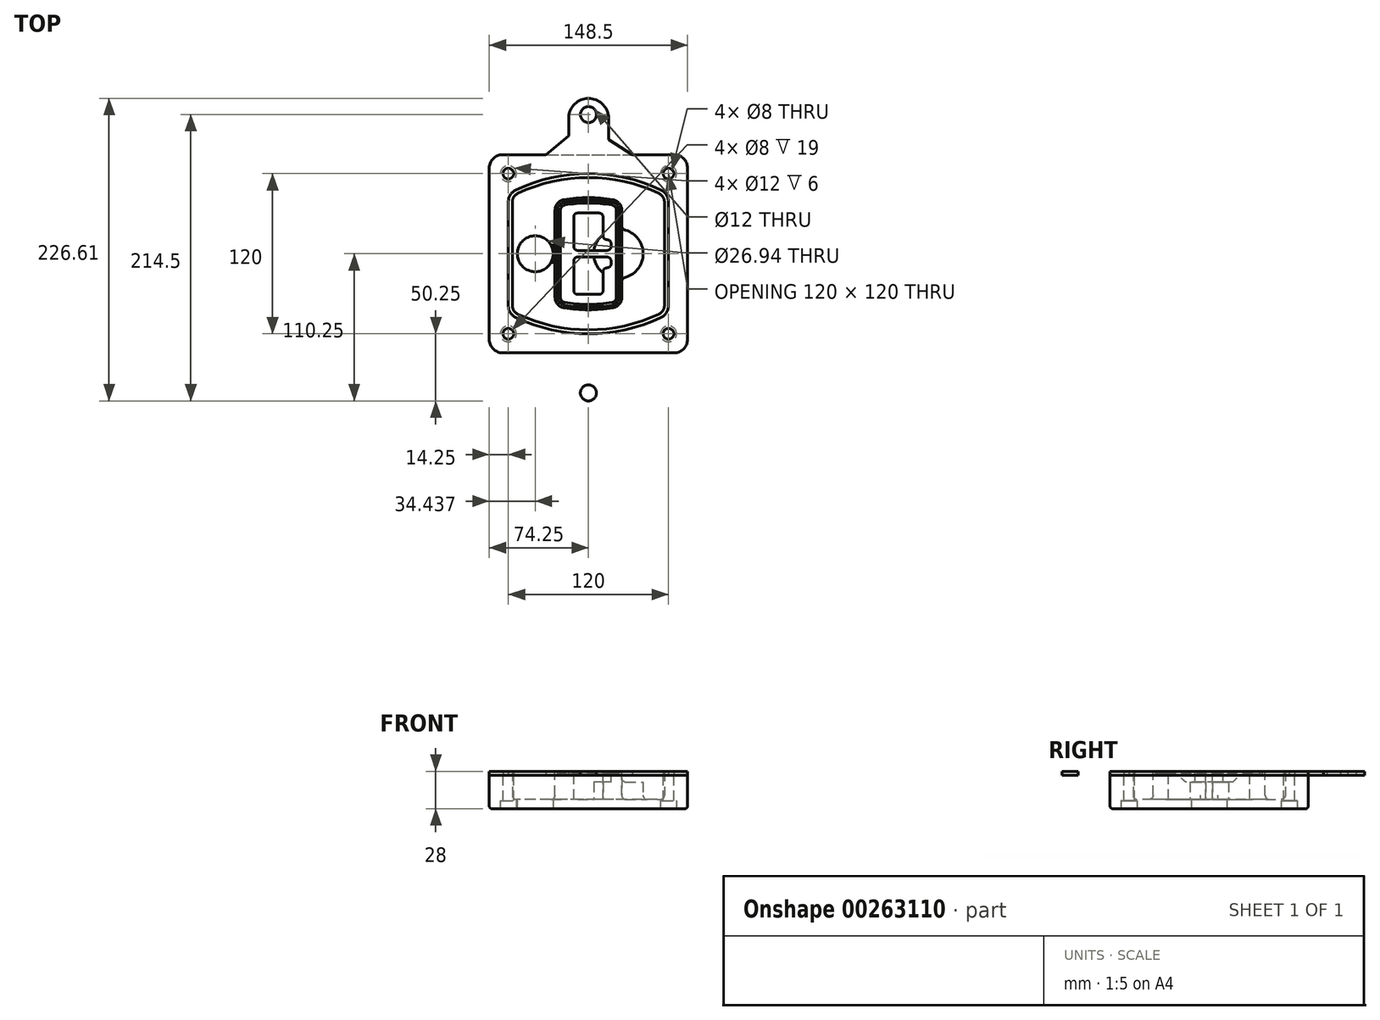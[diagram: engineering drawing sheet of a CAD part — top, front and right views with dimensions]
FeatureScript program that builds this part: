
annotation { "Feature Type Name" : "Feature", "Feature Type Description" : "" }
export const myFeature = defineFeature(function(context is Context, id is Id, definition is map)
    precondition{}
    {
        {
            var Q0;
            Q0=qCreatedBy(makeId("Top.planeOp"),FACE);
            var sketch = newSketch(context, id + "F0", { "sketchPlane" : qUnion([Q0])});
            skPoint(sketch, "E0.rect.middle", {"position": v(0, 0) * mm});
            skLineSegment(sketch, "E1.bottom", {"start": v(-64.25, -74.25) * mm, "end": v(64.25, -74.25) * mm});
            skLineSegment(sketch, "E1.top", {"start": v(-64.25, 74.25) * mm, "end": v(64.25, 74.25) * mm});
            skLineSegment(sketch, "E1.left", {"start": v(-74.25, -64.25) * mm, "end": v(-74.25, 64.25) * mm});
            skLineSegment(sketch, "E1.right", {"start": v(74.25, -64.25) * mm, "end": v(74.25, 64.25) * mm});
            skLineSegment(sketch, "E2", {"start": v(-74.25, 74.25) * mm, "end": v(74.25, -74.25) * mm, "construction": true});
            skLineSegment(sketch, "E3", {"start": v(74.25, 74.25) * mm, "end": v(-74.25, -74.25) * mm, "construction": true});
            skCircle(sketch, "E4", {"center": v(-60, 60) * mm, "radius": 4 * mm});
            skCircle(sketch, "E5", {"center": v(60, 60) * mm, "radius": 4 * mm});
            skCircle(sketch, "E6", {"center": v(60, -60) * mm, "radius": 4 * mm});
            skCircle(sketch, "E7", {"center": v(-60, -60) * mm, "radius": 4 * mm});
            skLineSegment(sketch, "E8", {"start": v(-60, 60) * mm, "end": v(60, 60) * mm, "construction": true});
            skLineSegment(sketch, "E9", {"start": v(60, 60) * mm, "end": v(60, -60) * mm, "construction": true});
            skLineSegment(sketch, "E10", {"start": v(60, -60) * mm, "end": v(-60, -60) * mm, "construction": true});
            skLineSegment(sketch, "E11", {"start": v(-60, -60) * mm, "end": v(-60, 60) * mm, "construction": true});
            skLineSegment(sketch, "E12", {"start": v(-60, 38.83) * mm, "end": v(-60, -38.83) * mm});
            skLineSegment(sketch, "E13", {"start": v(60, 38.83) * mm, "end": v(60, -38.83) * mm});
            skArc(sketch, "E14", {"start": v(54.26, 47.88) * mm, "mid": v(0, 60) * mm, "end": v(-54.26, 47.88) * mm});
            skArc(sketch, "E15", {"start": v(-54.26, -47.88) * mm, "mid": v(0, -60) * mm, "end": v(54.26, -47.88) * mm});
            skLineSegment(sketch, "E16", {"start": v(-60, 0) * mm, "end": v(60, 0) * mm, "construction": true});
            skPoint(sketch, "E17.visualSharp", {"position": v(-60, -45) * mm});
            skArc(sketch, "E17.filletArc", {"start": v(-60, -38.83) * mm, "mid": v(-58.44, -44.2) * mm, "end": v(-54.26, -47.88) * mm});
            skPoint(sketch, "E18.visualSharp", {"position": v(-60, 45) * mm});
            skArc(sketch, "E18.filletArc", {"start": v(-54.26, 47.88) * mm, "mid": v(-58.44, 44.2) * mm, "end": v(-60, 38.83) * mm});
            skPoint(sketch, "E19.visualSharp", {"position": v(60, 45) * mm});
            skArc(sketch, "E19.filletArc", {"start": v(60, 38.83) * mm, "mid": v(58.44, 44.2) * mm, "end": v(54.26, 47.88) * mm});
            skPoint(sketch, "E20.visualSharp", {"position": v(60, -45) * mm});
            skArc(sketch, "E20.filletArc", {"start": v(54.26, -47.88) * mm, "mid": v(58.44, -44.2) * mm, "end": v(60, -38.83) * mm});
            skPoint(sketch, "E21.visualSharp", {"position": v(-74.25, 74.25) * mm});
            skArc(sketch, "E21.filletArc", {"start": v(-64.25, 74.25) * mm, "mid": v(-71.32, 71.32) * mm, "end": v(-74.25, 64.25) * mm});
            skPoint(sketch, "E22.visualSharp", {"position": v(74.25, 74.25) * mm});
            skArc(sketch, "E22.filletArc", {"start": v(74.25, 64.25) * mm, "mid": v(71.32, 71.32) * mm, "end": v(64.25, 74.25) * mm});
            skPoint(sketch, "E23.visualSharp", {"position": v(74.25, -74.25) * mm});
            skArc(sketch, "E23.filletArc", {"start": v(64.25, -74.25) * mm, "mid": v(71.32, -71.32) * mm, "end": v(74.25, -64.25) * mm});
            skPoint(sketch, "E24.visualSharp", {"position": v(-74.25, -74.25) * mm});
            skArc(sketch, "E24.filletArc", {"start": v(-74.25, -64.25) * mm, "mid": v(-71.32, -71.32) * mm, "end": v(-64.25, -74.25) * mm});
            skArc(sketch, "E25.0", {"start": v(57, 38.83) * mm, "mid": v(55.9, 42.58) * mm, "end": v(52.98, 45.17) * mm});
            skLineSegment(sketch, "E25.1", {"start": v(57, 38.83) * mm, "end": v(57, -38.83) * mm});
            skArc(sketch, "E25.2", {"start": v(52.98, -45.17) * mm, "mid": v(55.9, -42.58) * mm, "end": v(57, -38.83) * mm});
            skArc(sketch, "E25.3", {"start": v(-52.98, -45.17) * mm, "mid": v(0, -57) * mm, "end": v(52.98, -45.17) * mm});
            skArc(sketch, "E25.4", {"start": v(-57, -38.83) * mm, "mid": v(-55.9, -42.58) * mm, "end": v(-52.98, -45.17) * mm});
            skArc(sketch, "E25.5", {"start": v(52.98, 45.17) * mm, "mid": v(0, 57) * mm, "end": v(-52.98, 45.17) * mm});
            skLineSegment(sketch, "E25.6", {"start": v(-57, 38.83) * mm, "end": v(-57, -38.83) * mm});
            skArc(sketch, "E25.7", {"start": v(-52.98, 45.17) * mm, "mid": v(-55.9, 42.58) * mm, "end": v(-57, 38.83) * mm});
            skArc(sketch, "E26.0", {"start": v(-55.96, 51.5) * mm, "mid": v(-61.82, 46.33) * mm, "end": v(-64, 38.83) * mm});
            skArc(sketch, "E26.1", {"start": v(55.96, 51.5) * mm, "mid": v(0, 64) * mm, "end": v(-55.96, 51.5) * mm});
            skArc(sketch, "E26.2", {"start": v(64, 38.83) * mm, "mid": v(61.82, 46.33) * mm, "end": v(55.96, 51.5) * mm});
            skLineSegment(sketch, "E26.3", {"start": v(64, 38.83) * mm, "end": v(64, -38.83) * mm});
            skArc(sketch, "E26.4", {"start": v(55.96, -51.5) * mm, "mid": v(61.82, -46.33) * mm, "end": v(64, -38.83) * mm});
            skLineSegment(sketch, "E26.5", {"start": v(-64, 38.83) * mm, "end": v(-64, -38.83) * mm});
            skArc(sketch, "E26.6", {"start": v(-55.96, -51.5) * mm, "mid": v(0, -64) * mm, "end": v(55.96, -51.5) * mm});
            skArc(sketch, "E26.7", {"start": v(-64, -38.83) * mm, "mid": v(-61.82, -46.33) * mm, "end": v(-55.96, -51.5) * mm});
            skSolve(sketch);
        }
        {
            var Q0;
            Q0=makeQuery(id+"F0.imprint","IMPRINT",FACE,{"disambiguationData":[TD([[makeQuery(id+"F0.imprint","IMPRINT",EDGE,{"derivedFrom":sQuery(id+"F0.wireOp",EDGE,"E1.bottom")}),1.0]])]});
            var Q1;
            Q1=makeQuery(id+"F0.imprint","IMPRINT",FACE,{"disambiguationData":[TD([[makeQuery(id+"F0.imprint","IMPRINT",EDGE,{"derivedFrom":sQuery(id+"F0.wireOp",EDGE,"E12")}),1.0]])]});
            var Q2;
            Q2=makeQuery(id+"F0.imprint","IMPRINT",FACE,{"disambiguationData":[TD([[makeQuery(id+"F0.imprint","IMPRINT",EDGE,{"derivedFrom":sQuery(id+"F0.wireOp",EDGE,"E25.0")}),1.0]])]});
            var Q3;
            Q3=makeQuery(id+"F0.imprint","IMPRINT",FACE,{"disambiguationData":[TD([[makeQuery(id+"F0.imprint","IMPRINT",EDGE,{"derivedFrom":sQuery(id+"F0.wireOp",EDGE,"E12")}),-1.0]])]});
            extrude(context, id + "F1", {"entities" : qUnion([Q0, Q1, Q2, Q3]), "oppositeDirection" : true, "depth" : 25 * mm});
        }
        {
            var Q0;
            Q0=makeQuery(id+"F0.imprint","IMPRINT",FACE,{"disambiguationData":[TD([[makeQuery(id+"F0.imprint","IMPRINT",EDGE,{"derivedFrom":sQuery(id+"F0.wireOp",EDGE,"E12")}),1.0]])]});
            extrude(context, id + "F2", {"entities" : qUnion([Q0]), "operationType" : NewBodyOperationType.ADD, "depth" : 3 * mm});
        }
        {
            var Q0;
            Q0=makeQuery(id+"F0.imprint","IMPRINT",FACE,{"disambiguationData":[TD([[makeQuery(id+"F0.imprint","IMPRINT",EDGE,{"derivedFrom":sQuery(id+"F0.wireOp",EDGE,"E25.0")}),1.0]])]});
            extrude(context, id + "F3", {"entities" : qUnion([Q0]), "operationType" : NewBodyOperationType.REMOVE, "oppositeDirection" : true, "depth" : 18 * mm});
        }
        {
            var Q0;
            Q0=makeQuery(id+"F2.opExtrude","CAP_FACE",FACE,{"disambiguationData":[OSD([sQuery(id+"F0.wireOp",EDGE,"E12"),sQuery(id+"F0.wireOp",EDGE,"E13"),sQuery(id+"F0.wireOp",EDGE,"E14"),sQuery(id+"F0.wireOp",EDGE,"E15"),sQuery(id+"F0.wireOp",EDGE,"E17.filletArc"),sQuery(id+"F0.wireOp",EDGE,"E18.filletArc"),sQuery(id+"F0.wireOp",EDGE,"E19.filletArc"),sQuery(id+"F0.wireOp",EDGE,"E20.filletArc"),sQuery(id+"F0.wireOp",EDGE,"E25.0"),sQuery(id+"F0.wireOp",EDGE,"E25.1"),sQuery(id+"F0.wireOp",EDGE,"E25.2"),sQuery(id+"F0.wireOp",EDGE,"E25.3"),sQuery(id+"F0.wireOp",EDGE,"E25.4"),sQuery(id+"F0.wireOp",EDGE,"E25.5"),sQuery(id+"F0.wireOp",EDGE,"E25.6"),sQuery(id+"F0.wireOp",EDGE,"E25.7")])],"isStart":false});
            var sketch = newSketch(context, id + "F4", { "sketchPlane" : qUnion([Q0])});
            skArc(sketch, "E27.0", {"start": v(-18.34, -40.45) * mm, "mid": v(0, -42) * mm, "end": v(18.34, -40.45) * mm});
            skArc(sketch, "E28.0", {"start": v(18.34, 40.45) * mm, "mid": v(0, 42) * mm, "end": v(-18.34, 40.45) * mm});
            skLineSegment(sketch, "E29", {"start": v(-25, 32.57) * mm, "end": v(-25, -32.57) * mm});
            skLineSegment(sketch, "E30", {"start": v(25, 32.57) * mm, "end": v(25, -32.57) * mm});
            skLineSegment(sketch, "E31", {"start": v(-25, 39.1) * mm, "end": v(25, 39.1) * mm, "construction": true});
            skLineSegment(sketch, "E32", {"start": v(-25, -39.1) * mm, "end": v(25, -39.1) * mm, "construction": true});
            skPoint(sketch, "E33.visualSharp", {"position": v(-25, 39.1) * mm});
            skArc(sketch, "E33.filletArc", {"start": v(-18.34, 40.45) * mm, "mid": v(-23.11, 37.73) * mm, "end": v(-25, 32.57) * mm});
            skPoint(sketch, "E34.visualSharp", {"position": v(25, 39.1) * mm});
            skArc(sketch, "E34.filletArc", {"start": v(25, 32.57) * mm, "mid": v(23.11, 37.73) * mm, "end": v(18.34, 40.45) * mm});
            skPoint(sketch, "E35.visualSharp", {"position": v(25, -39.1) * mm});
            skArc(sketch, "E35.filletArc", {"start": v(18.34, -40.45) * mm, "mid": v(23.11, -37.73) * mm, "end": v(25, -32.57) * mm});
            skPoint(sketch, "E36.visualSharp", {"position": v(-25, -39.1) * mm});
            skArc(sketch, "E36.filletArc", {"start": v(-25, -32.57) * mm, "mid": v(-23.11, -37.73) * mm, "end": v(-18.34, -40.45) * mm});
            skArc(sketch, "E37.0", {"start": v(52.98, 45.17) * mm, "mid": v(0, 57) * mm, "end": v(-52.98, 45.17) * mm});
            skArc(sketch, "E37.1", {"start": v(-52.98, 45.17) * mm, "mid": v(-55.9, 42.58) * mm, "end": v(-57, 38.83) * mm});
            skLineSegment(sketch, "E37.2", {"start": v(-57, 38.83) * mm, "end": v(-57, -38.83) * mm});
            skArc(sketch, "E37.3", {"start": v(-57, -38.83) * mm, "mid": v(-55.9, -42.58) * mm, "end": v(-52.98, -45.17) * mm});
            skArc(sketch, "E37.4", {"start": v(-52.98, -45.17) * mm, "mid": v(0, -57) * mm, "end": v(52.98, -45.17) * mm});
            skArc(sketch, "E37.5", {"start": v(52.98, -45.17) * mm, "mid": v(55.9, -42.58) * mm, "end": v(57, -38.83) * mm});
            skLineSegment(sketch, "E37.6", {"start": v(57, 38.83) * mm, "end": v(57, -38.83) * mm});
            skArc(sketch, "E37.7", {"start": v(57, 38.83) * mm, "mid": v(55.9, 42.58) * mm, "end": v(52.98, 45.17) * mm});
            skLineSegment(sketch, "E38.0", {"start": v(23, 32.57) * mm, "end": v(23, -32.57) * mm});
            skArc(sketch, "E38.1", {"start": v(18, -38.48) * mm, "mid": v(21.58, -36.44) * mm, "end": v(23, -32.57) * mm});
            skArc(sketch, "E38.2", {"start": v(-18, -38.48) * mm, "mid": v(0, -40) * mm, "end": v(18, -38.48) * mm});
            skArc(sketch, "E38.3", {"start": v(-23, -32.57) * mm, "mid": v(-21.58, -36.44) * mm, "end": v(-18, -38.48) * mm});
            skLineSegment(sketch, "E38.4", {"start": v(-23, 32.57) * mm, "end": v(-23, -32.57) * mm});
            skArc(sketch, "E38.5", {"start": v(23, 32.57) * mm, "mid": v(21.58, 36.44) * mm, "end": v(18, 38.48) * mm});
            skArc(sketch, "E38.6", {"start": v(-18, 38.48) * mm, "mid": v(-21.58, 36.44) * mm, "end": v(-23, 32.57) * mm});
            skArc(sketch, "E38.7", {"start": v(18, 38.48) * mm, "mid": v(0, 40) * mm, "end": v(-18, 38.48) * mm});
            skArc(sketch, "E39.0", {"start": v(21, 32.57) * mm, "mid": v(20.06, 35.15) * mm, "end": v(17.67, 36.5) * mm});
            skLineSegment(sketch, "E39.1", {"start": v(21, 32.57) * mm, "end": v(21, -32.57) * mm});
            skArc(sketch, "E39.2", {"start": v(17.67, -36.5) * mm, "mid": v(20.06, -35.15) * mm, "end": v(21, -32.57) * mm});
            skArc(sketch, "E39.3", {"start": v(-17.67, -36.5) * mm, "mid": v(0, -38) * mm, "end": v(17.67, -36.5) * mm});
            skArc(sketch, "E39.4", {"start": v(-21, -32.57) * mm, "mid": v(-20.06, -35.15) * mm, "end": v(-17.67, -36.5) * mm});
            skArc(sketch, "E39.5", {"start": v(17.67, 36.5) * mm, "mid": v(0, 38) * mm, "end": v(-17.67, 36.5) * mm});
            skLineSegment(sketch, "E39.6", {"start": v(-21, 32.57) * mm, "end": v(-21, -32.57) * mm});
            skArc(sketch, "E39.7", {"start": v(-17.67, 36.5) * mm, "mid": v(-20.06, 35.15) * mm, "end": v(-21, 32.57) * mm});
            skLineSegment(sketch, "E40", {"start": v(-25, 0) * mm, "end": v(25, 0) * mm, "construction": true});
            skLineSegment(sketch, "E41", {"start": v(-11, 5.5) * mm, "end": v(-11, 27.5) * mm});
            skLineSegment(sketch, "E42", {"start": v(-8, 30.5) * mm, "end": v(8, 30.5) * mm});
            skLineSegment(sketch, "E43", {"start": v(11, 27.5) * mm, "end": v(11, 13.5) * mm});
            skLineSegment(sketch, "E44", {"start": v(14, 10.5) * mm, "end": v(14, 10.5) * mm});
            skLineSegment(sketch, "E45", {"start": v(17, 7.5) * mm, "end": v(17, 5.5) * mm});
            skLineSegment(sketch, "E46", {"start": v(14, 2.5) * mm, "end": v(-8, 2.5) * mm});
            skPoint(sketch, "E47.visualSharp", {"position": v(-11, 30.5) * mm});
            skArc(sketch, "E47.filletArc", {"start": v(-8, 30.5) * mm, "mid": v(-10.12, 29.62) * mm, "end": v(-11, 27.5) * mm});
            skPoint(sketch, "E48.visualSharp", {"position": v(11, 30.5) * mm});
            skArc(sketch, "E48.filletArc", {"start": v(11, 27.5) * mm, "mid": v(10.12, 29.62) * mm, "end": v(8, 30.5) * mm});
            skPoint(sketch, "E49.visualSharp", {"position": v(11, 10.5) * mm});
            skArc(sketch, "E49.filletArc", {"start": v(11, 13.5) * mm, "mid": v(11.88, 11.38) * mm, "end": v(14, 10.5) * mm});
            skPoint(sketch, "E50.visualSharp", {"position": v(17, 10.5) * mm});
            skArc(sketch, "E50.filletArc", {"start": v(17, 7.5) * mm, "mid": v(16.12, 9.62) * mm, "end": v(14, 10.5) * mm});
            skPoint(sketch, "E51.visualSharp", {"position": v(17, 2.5) * mm});
            skArc(sketch, "E51.filletArc", {"start": v(14, 2.5) * mm, "mid": v(16.12, 3.38) * mm, "end": v(17, 5.5) * mm});
            skPoint(sketch, "E52.visualSharp", {"position": v(-11, 2.5) * mm});
            skArc(sketch, "E52.filletArc", {"start": v(-11, 5.5) * mm, "mid": v(-10.12, 3.38) * mm, "end": v(-8, 2.5) * mm});
            skLineSegment(sketch, "E53.0.MirrorCS", {"start": v(14, -2.5) * mm, "end": v(-8, -2.5) * mm});
            skArc(sketch, "E54.0.MirrorCS", {"start": v(-11, -5.5) * mm, "mid": v(-10.12, -3.38) * mm, "end": v(-8, -2.5) * mm});
            skLineSegment(sketch, "E55.0.MirrorCS", {"start": v(-11, -5.5) * mm, "end": v(-11, -27.5) * mm});
            skArc(sketch, "E56.0.MirrorCS", {"start": v(-8, -30.5) * mm, "mid": v(-10.12, -29.62) * mm, "end": v(-11, -27.5) * mm});
            skLineSegment(sketch, "E57.0.MirrorCS", {"start": v(-8, -30.5) * mm, "end": v(8, -30.5) * mm});
            skArc(sketch, "E58.0.MirrorCS", {"start": v(11, -27.5) * mm, "mid": v(10.12, -29.62) * mm, "end": v(8, -30.5) * mm});
            skLineSegment(sketch, "E59.0.MirrorCS", {"start": v(11, -27.5) * mm, "end": v(11, -13.5) * mm});
            skArc(sketch, "E60.0.MirrorCS", {"start": v(11, -13.5) * mm, "mid": v(11.88, -11.38) * mm, "end": v(14, -10.5) * mm});
            skArc(sketch, "E61.0.MirrorCS", {"start": v(17, -7.5) * mm, "mid": v(16.12, -9.62) * mm, "end": v(14, -10.5) * mm});
            skLineSegment(sketch, "E62.0.MirrorCS", {"start": v(17, -7.5) * mm, "end": v(17, -5.5) * mm});
            skArc(sketch, "E63.0.MirrorCS", {"start": v(14, -2.5) * mm, "mid": v(16.12, -3.38) * mm, "end": v(17, -5.5) * mm});
            skSolve(sketch);
        }
        {
            var Q0;
            Q0=makeQuery(id+"F4.imprint","IMPRINT",FACE,{"disambiguationData":[TD([[makeQuery(id+"F4.imprint","IMPRINT",EDGE,{"derivedFrom":sQuery(id+"F4.wireOp",EDGE,"E27.0")}),1.0]])]});
            var Q1;
            Q1=makeQuery(id+"F4.imprint","IMPRINT",FACE,{"disambiguationData":[TD([[makeQuery(id+"F4.imprint","IMPRINT",EDGE,{"derivedFrom":sQuery(id+"F4.wireOp",EDGE,"E38.0")}),-1.0]])]});
            var Q2;
            Q2=makeQuery(id+"F4.imprint","IMPRINT",FACE,{"disambiguationData":[TD([[makeQuery(id+"F4.imprint","IMPRINT",EDGE,{"derivedFrom":sQuery(id+"F4.wireOp",EDGE,"E39.0")}),1.0]])]});
            extrude(context, id + "F5", {"entities" : qUnion([Q0, Q1, Q2]), "operationType" : NewBodyOperationType.ADD, "endBound" : BoundingType.UP_TO_NEXT, "oppositeDirection" : true, "depth" : 25 * mm});
        }
        {
            var Q0;
            Q0=makeQuery(id+"F4.imprint","IMPRINT",FACE,{"disambiguationData":[TD([[makeQuery(id+"F4.imprint","IMPRINT",EDGE,{"derivedFrom":sQuery(id+"F4.wireOp",EDGE,"E38.0")}),-1.0]])]});
            extrude(context, id + "F6", {"entities" : qUnion([Q0]), "operationType" : NewBodyOperationType.REMOVE, "oppositeDirection" : true, "depth" : 2 * mm});
        }
        {
            var Q0;
            Q0=makeQuery(id+"F1.opExtrude","CAP_FACE",FACE,{"disambiguationData":[OSD([sQuery(id+"F0.wireOp",EDGE,"E1.bottom"),sQuery(id+"F0.wireOp",EDGE,"E1.top"),sQuery(id+"F0.wireOp",EDGE,"E1.left"),sQuery(id+"F0.wireOp",EDGE,"E1.right"),sQuery(id+"F0.wireOp",EDGE,"E4"),sQuery(id+"F0.wireOp",EDGE,"E5"),sQuery(id+"F0.wireOp",EDGE,"E6"),sQuery(id+"F0.wireOp",EDGE,"E7"),sQuery(id+"F0.wireOp",EDGE,"E21.filletArc"),sQuery(id+"F0.wireOp",EDGE,"E22.filletArc"),sQuery(id+"F0.wireOp",EDGE,"E23.filletArc"),sQuery(id+"F0.wireOp",EDGE,"E24.filletArc")])],"isStart":false});
            var sketch = newSketch(context, id + "F7", { "sketchPlane" : qUnion([Q0])});
            skCircle(sketch, "E64", {"center": v(22.5, 0) * mm, "radius": 13.47 * mm});
            skCircle(sketch, "E65", {"center": v(-39.81, 0) * mm, "radius": 13.47 * mm});
            skLineSegment(sketch, "E66", {"start": v(74.25, 0) * mm, "end": v(-74.25, 0) * mm});
            skCircle(sketch, "E67", {"center": v(22.5, 0) * mm, "radius": 18.47 * mm});
            skCircle(sketch, "E68", {"center": v(60, -60) * mm, "radius": 6 * mm});
            skCircle(sketch, "E69", {"center": v(-60, -60) * mm, "radius": 6 * mm});
            skCircle(sketch, "E70", {"center": v(-60, 60) * mm, "radius": 6 * mm});
            skCircle(sketch, "E71", {"center": v(60, 60) * mm, "radius": 6 * mm});
            skSolve(sketch);
        }
        {
            var Q0;
            {var subQ0=sQuery(id+"F7.wireOp",EDGE,"E66");var subQ1=sQuery(id+"F7.wireOp",EDGE,"E64");var subQ3=makeQuery(id+"F7.imprint","INTERSECT",VERTEX,{"disambiguationData":[OD(0.0)],"derivedFrom":[subQ1,subQ0]});Q0=makeQuery(id+"F7.imprint","IMPRINT",FACE,{"disambiguationData":[TD([[makeQuery(id+"F7.imprint","IMPRINT",EDGE,{"disambiguationData":[TD([[subQ3,-1.0]])],"derivedFrom":subQ1}),1.0]])]});}
            var Q1;
            {var subQ0=sQuery(id+"F7.wireOp",EDGE,"E66");var subQ1=sQuery(id+"F7.wireOp",EDGE,"E64");var subQ3=makeQuery(id+"F7.imprint","INTERSECT",VERTEX,{"disambiguationData":[OD(0.0)],"derivedFrom":[subQ1,subQ0]});Q1=makeQuery(id+"F7.imprint","IMPRINT",FACE,{"disambiguationData":[TD([[makeQuery(id+"F7.imprint","IMPRINT",EDGE,{"disambiguationData":[TD([[subQ3,1.0]])],"derivedFrom":subQ1}),1.0]])]});}
            extrude(context, id + "F8", {"entities" : qUnion([Q0, Q1]), "operationType" : NewBodyOperationType.REMOVE, "oppositeDirection" : true, "depth" : 16 * mm});
        }
        {
            var Q0;
            {var subQ0=sQuery(id+"F7.wireOp",EDGE,"E66");var subQ1=sQuery(id+"F7.wireOp",EDGE,"E65");var subQ3=makeQuery(id+"F7.imprint","INTERSECT",VERTEX,{"disambiguationData":[OD(0.0)],"derivedFrom":[subQ1,subQ0]});Q0=makeQuery(id+"F7.imprint","IMPRINT",FACE,{"disambiguationData":[TD([[makeQuery(id+"F7.imprint","IMPRINT",EDGE,{"disambiguationData":[TD([[subQ3,-1.0]])],"derivedFrom":subQ1}),1.0]])]});}
            var Q1;
            {var subQ0=sQuery(id+"F7.wireOp",EDGE,"E66");var subQ1=sQuery(id+"F7.wireOp",EDGE,"E65");var subQ3=makeQuery(id+"F7.imprint","INTERSECT",VERTEX,{"disambiguationData":[OD(0.0)],"derivedFrom":[subQ1,subQ0]});Q1=makeQuery(id+"F7.imprint","IMPRINT",FACE,{"disambiguationData":[TD([[makeQuery(id+"F7.imprint","IMPRINT",EDGE,{"disambiguationData":[TD([[subQ3,1.0]])],"derivedFrom":subQ1}),1.0]])]});}
            extrude(context, id + "F9", {"entities" : qUnion([Q0, Q1]), "operationType" : NewBodyOperationType.REMOVE, "oppositeDirection" : true, "depth" : 25 * mm});
        }
        {
            var Q0;
            {var subQ1=sQuery(id+"F7.wireOp",EDGE,"E66");var subQ4=sQuery(id+"F7.wireOp",EDGE,"E64");var subQ6=makeQuery(id+"F7.imprint","INTERSECT",VERTEX,{"disambiguationData":[OD(0.0)],"derivedFrom":[subQ4,subQ1]});Q0=makeQuery(id+"F7.imprint","IMPRINT",FACE,{"disambiguationData":[TD([[makeQuery(id+"F7.imprint","IMPRINT",EDGE,{"disambiguationData":[TD([[subQ6,-1.0]])],"derivedFrom":subQ4}),-1.0]])]});}
            var Q1;
            {var subQ0=sQuery(id+"F7.wireOp",EDGE,"E66");var subQ1=sQuery(id+"F7.wireOp",EDGE,"E64");var subQ3=makeQuery(id+"F7.imprint","INTERSECT",VERTEX,{"disambiguationData":[OD(0.0)],"derivedFrom":[subQ1,subQ0]});Q1=makeQuery(id+"F7.imprint","IMPRINT",FACE,{"disambiguationData":[TD([[makeQuery(id+"F7.imprint","IMPRINT",EDGE,{"disambiguationData":[TD([[subQ3,-1.0]])],"derivedFrom":subQ1}),1.0]])]});}
            var Q2;
            {var subQ0=sQuery(id+"F7.wireOp",EDGE,"E66");var subQ1=sQuery(id+"F7.wireOp",EDGE,"E64");var subQ3=makeQuery(id+"F7.imprint","INTERSECT",VERTEX,{"disambiguationData":[OD(0.0)],"derivedFrom":[subQ1,subQ0]});Q2=makeQuery(id+"F7.imprint","IMPRINT",FACE,{"disambiguationData":[TD([[makeQuery(id+"F7.imprint","IMPRINT",EDGE,{"disambiguationData":[TD([[subQ3,1.0]])],"derivedFrom":subQ1}),1.0]])]});}
            var Q3;
            {var subQ1=sQuery(id+"F7.wireOp",EDGE,"E66");var subQ4=sQuery(id+"F7.wireOp",EDGE,"E64");var subQ6=makeQuery(id+"F7.imprint","INTERSECT",VERTEX,{"disambiguationData":[OD(0.0)],"derivedFrom":[subQ4,subQ1]});Q3=makeQuery(id+"F7.imprint","IMPRINT",FACE,{"disambiguationData":[TD([[makeQuery(id+"F7.imprint","IMPRINT",EDGE,{"disambiguationData":[TD([[subQ6,1.0]])],"derivedFrom":subQ4}),-1.0]])]});}
            extrude(context, id + "F10", {"entities" : qUnion([Q0, Q1, Q2, Q3]), "operationType" : NewBodyOperationType.ADD, "oppositeDirection" : true, "depth" : 20 * mm});
        }
        {
            var Q0;
            Q0=makeQuery(id+"F7.imprint","IMPRINT",FACE,{"disambiguationData":[TD([[makeQuery(id+"F7.imprint","IMPRINT",EDGE,{"derivedFrom":sQuery(id+"F7.wireOp",EDGE,"E68")}),1.0]])]});
            var Q1;
            Q1=makeQuery(id+"F7.imprint","IMPRINT",FACE,{"disambiguationData":[TD([[makeQuery(id+"F7.imprint","IMPRINT",EDGE,{"derivedFrom":makeQuery(id+"F1.opExtrude","CAP_EDGE",EDGE,{"disambiguationData":[OSD([sQuery(id+"F0.wireOp",EDGE,"E5")])],"isStart":false})}),-1.0]])]});
            var Q2;
            Q2=makeQuery(id+"F7.imprint","IMPRINT",FACE,{"disambiguationData":[TD([[makeQuery(id+"F7.imprint","IMPRINT",EDGE,{"derivedFrom":sQuery(id+"F7.wireOp",EDGE,"E69")}),1.0]])]});
            var Q3;
            Q3=makeQuery(id+"F7.imprint","IMPRINT",FACE,{"disambiguationData":[TD([[makeQuery(id+"F7.imprint","IMPRINT",EDGE,{"derivedFrom":makeQuery(id+"F1.opExtrude","CAP_EDGE",EDGE,{"disambiguationData":[OSD([sQuery(id+"F0.wireOp",EDGE,"E4")])],"isStart":false})}),-1.0]])]});
            var Q4;
            Q4=makeQuery(id+"F7.imprint","IMPRINT",FACE,{"disambiguationData":[TD([[makeQuery(id+"F7.imprint","IMPRINT",EDGE,{"derivedFrom":sQuery(id+"F7.wireOp",EDGE,"E70")}),1.0]])]});
            var Q5;
            Q5=makeQuery(id+"F7.imprint","IMPRINT",FACE,{"disambiguationData":[TD([[makeQuery(id+"F7.imprint","IMPRINT",EDGE,{"derivedFrom":makeQuery(id+"F1.opExtrude","CAP_EDGE",EDGE,{"disambiguationData":[OSD([sQuery(id+"F0.wireOp",EDGE,"E7")])],"isStart":false})}),-1.0]])]});
            var Q6;
            Q6=makeQuery(id+"F7.imprint","IMPRINT",FACE,{"disambiguationData":[TD([[makeQuery(id+"F7.imprint","IMPRINT",EDGE,{"derivedFrom":sQuery(id+"F7.wireOp",EDGE,"E71")}),1.0]])]});
            var Q7;
            Q7=makeQuery(id+"F7.imprint","IMPRINT",FACE,{"disambiguationData":[TD([[makeQuery(id+"F7.imprint","IMPRINT",EDGE,{"derivedFrom":makeQuery(id+"F1.opExtrude","CAP_EDGE",EDGE,{"disambiguationData":[OSD([sQuery(id+"F0.wireOp",EDGE,"E6")])],"isStart":false})}),-1.0]])]});
            extrude(context, id + "F11", {"entities" : qUnion([Q0, Q1, Q2, Q3, Q4, Q5, Q6, Q7]), "operationType" : NewBodyOperationType.REMOVE, "oppositeDirection" : true, "depth" : 6 * mm});
        }
        {
            var Q0;
            Q0=makeQuery(id+"F3.boolean.opBoolean","COPY",EDGE,{"derivedFrom":makeQuery(id+"F3.opExtrude","CAP_EDGE",EDGE,{"disambiguationData":[OSD([sQuery(id+"F0.wireOp",EDGE,"E25.6")])],"isStart":false})});
            var Q1;
            Q1=makeQuery(id+"F10.boolean.opBoolean","INTERSECT",EDGE,{"derivedFrom":[makeQuery(id+"F5.opExtrude","SWEPT_FACE",FACE,{"disambiguationData":[OSD([sQuery(id+"F4.wireOp",EDGE,"E30")])]}),makeQuery(id+"F10.opExtrude","CAP_FACE",FACE,{"disambiguationData":[OSD([sQuery(id+"F7.wireOp",EDGE,"E67")])],"isStart":false})]});
            var Q2;
            Q2=makeQuery(id+"F10.boolean.opBoolean","INTERSECT",EDGE,{"disambiguationData":[OD(1.0)],"derivedFrom":[makeQuery(id+"F5.opExtrude","SWEPT_FACE",FACE,{"disambiguationData":[OSD([sQuery(id+"F4.wireOp",EDGE,"E30")])]}),makeQuery(id+"F10.opExtrude","SWEPT_FACE",FACE,{"disambiguationData":[OSD([sQuery(id+"F7.wireOp",EDGE,"E67")])]})]});
            var Q3;
            {var subQ1=sQuery(id+"F4.wireOp",EDGE,"E30");var subQ4=makeQuery(id+"F5.opExtrude","CAP_EDGE",EDGE,{"disambiguationData":[OSD([subQ1])],"isStart":false});Q3=qUnion([makeQuery(id+"F8.boolean.opBoolean","SPLIT",EDGE,{"disambiguationData":[TD([makeQuery(id+"F5.opExtrude","SWEPT_FACE",FACE,{"disambiguationData":[OSD([sQuery(id+"F4.wireOp",EDGE,"E34.filletArc")])]})])],"derivedFrom":subQ4}),makeQuery(id+"F8.boolean.opBoolean","SPLIT",EDGE,{"disambiguationData":[TD([makeQuery(id+"F5.opExtrude","SWEPT_FACE",FACE,{"disambiguationData":[OSD([sQuery(id+"F4.wireOp",EDGE,"E35.filletArc")])]})])],"derivedFrom":subQ4})]);}
            var Q4;
            {var subQ0=sQuery(id+"F0.wireOp",EDGE,"E25.7");var subQ1=sQuery(id+"F0.wireOp",EDGE,"E25.1");var subQ2=sQuery(id+"F0.wireOp",EDGE,"E25.6");var subQ3=sQuery(id+"F0.wireOp",EDGE,"E25.5");var subQ4=sQuery(id+"F0.wireOp",EDGE,"E25.4");var subQ5=sQuery(id+"F0.wireOp",EDGE,"E25.0");var subQ6=sQuery(id+"F0.wireOp",EDGE,"E25.2");var subQ7=sQuery(id+"F0.wireOp",EDGE,"E25.3");Q4=makeQuery(id+"F10.boolean.opBoolean","INTERSECT",EDGE,{"derivedFrom":[makeQuery(id+"F5.boolean.opBoolean","SPLIT",FACE,{"disambiguationData":[TD([makeQuery(id+"F2.opExtrude","SWEPT_FACE",FACE,{"disambiguationData":[OSD([subQ5])]})])],"derivedFrom":makeQuery(id+"F3.boolean.opBoolean","COPY",FACE,{"derivedFrom":makeQuery(id+"F3.opExtrude","CAP_FACE",FACE,{"disambiguationData":[OSD([subQ5,subQ1,subQ6,subQ7,subQ4,subQ3,subQ2,subQ0])],"isStart":false})})}),makeQuery(id+"F10.opExtrude","SWEPT_FACE",FACE,{"disambiguationData":[OSD([sQuery(id+"F7.wireOp",EDGE,"E67")])]})]});}
            var Q5;
            Q5=makeQuery(id+"F10.boolean.opBoolean","INTERSECT",EDGE,{"disambiguationData":[OD(0.0)],"derivedFrom":[makeQuery(id+"F5.opExtrude","SWEPT_FACE",FACE,{"disambiguationData":[OSD([sQuery(id+"F4.wireOp",EDGE,"E30")])]}),makeQuery(id+"F10.opExtrude","SWEPT_FACE",FACE,{"disambiguationData":[OSD([sQuery(id+"F7.wireOp",EDGE,"E67")])]})]});
            fillet(context, id + "F12", {"entities" : qUnion([Q0, Q1, Q2, Q3, Q4, Q5]), "radius" : 3 * mm, "tangentPropagation" : true, "allowEdgeOverflow" : false});
        }
        {
            var Q0;
            Q0=makeQuery(id+"F1.opExtrude","CAP_EDGE",EDGE,{"disambiguationData":[OSD([sQuery(id+"F0.wireOp",EDGE,"E1.bottom")])],"isStart":false});
            fillet(context, id + "F13", {"entities" : qUnion([Q0]), "radius" : 2 * mm, "tangentPropagation" : true, "allowEdgeOverflow" : false});
        }
        {
            var Q0;
            {var subQ0=sQuery(id+"F0.wireOp",EDGE,"E22.filletArc");var subQ1=sQuery(id+"F0.wireOp",EDGE,"E7");var subQ2=sQuery(id+"F0.wireOp",EDGE,"E6");var subQ3=sQuery(id+"F0.wireOp",EDGE,"E5");var subQ4=sQuery(id+"F0.wireOp",EDGE,"E4");var subQ5=sQuery(id+"F0.wireOp",EDGE,"E1.bottom");var subQ6=sQuery(id+"F0.wireOp",EDGE,"E21.filletArc");var subQ7=sQuery(id+"F0.wireOp",EDGE,"E1.top");var subQ8=sQuery(id+"F0.wireOp",EDGE,"E1.left");var subQ9=sQuery(id+"F0.wireOp",EDGE,"E1.right");var subQ10=sQuery(id+"F0.wireOp",EDGE,"E23.filletArc");var subQ11=sQuery(id+"F0.wireOp",EDGE,"E24.filletArc");Q0=makeQuery(id+"F2.boolean.opBoolean","SPLIT",FACE,{"disambiguationData":[TD([makeQuery(id+"F1.opExtrude","SWEPT_FACE",FACE,{"disambiguationData":[OSD([subQ5])]})])],"derivedFrom":makeQuery(id+"F1.opExtrude","CAP_FACE",FACE,{"disambiguationData":[OSD([subQ5,subQ7,subQ8,subQ9,subQ4,subQ3,subQ2,subQ1,subQ6,subQ0,subQ10,subQ11])],"isStart":true})});}
            var sketch = newSketch(context, id + "F14", { "sketchPlane" : qUnion([Q0])});
            skLineSegment(sketch, "E72", {"start": v(0, -74.25) * mm, "end": v(0, -104.25) * mm});
            skPoint(sketch, "E72.endSnap0", {"position": v(0, -74.25) * mm});
            skLineSegment(sketch, "E73", {"start": v(0, 74.25) * mm, "end": v(0, 104.25) * mm, "construction": true});
            skCircle(sketch, "E74", {"center": v(0, 104.25) * mm, "radius": 6 * mm});
            skLineSegment(sketch, "E75", {"start": v(-31.94, 74.25) * mm, "end": v(-14.68, 88.34) * mm});
            skLineSegment(sketch, "E76", {"start": v(32.9, 74.25) * mm, "end": v(15.13, 85.58) * mm});
            skLineSegment(sketch, "E77", {"start": v(-14.68, 88.34) * mm, "end": v(-14.68, 103.76) * mm});
            skLineSegment(sketch, "E78", {"start": v(15.13, 85.58) * mm, "end": v(15.13, 101.3) * mm});
            skArc(sketch, "E79", {"start": v(15.13, 101.3) * mm, "mid": v(1.36, 116.3) * mm, "end": v(-14.68, 103.76) * mm});
            skPoint(sketch, "E80.startSnap0", {"position": v(-74.25, 0) * mm});
            skLineSegment(sketch, "E81", {"start": v(-95, 0) * mm, "end": v(85.45, 0) * mm, "construction": true});
            skPoint(sketch, "E81.startSnap0", {"position": v(-60, 0) * mm});
            skPoint(sketch, "E81.endSnap0", {"position": v(74.25, 0) * mm});
            skLineSegment(sketch, "E82.MirrorCS", {"start": v(0, -74.25) * mm, "end": v(0, -104.25) * mm, "construction": true});
            skCircle(sketch, "E83.MirrorC", {"center": v(0, -104.25) * mm, "radius": 6 * mm});
            skLineSegment(sketch, "E84.MirrorCS", {"start": v(-31.94, -74.25) * mm, "end": v(-14.68, -88.34) * mm});
            skLineSegment(sketch, "E85.MirrorCS", {"start": v(32.9, -74.25) * mm, "end": v(15.13, -85.58) * mm});
            skLineSegment(sketch, "E86.MirrorCS", {"start": v(-14.68, -88.34) * mm, "end": v(-14.68, -103.76) * mm});
            skLineSegment(sketch, "E87.MirrorCS", {"start": v(15.13, -85.58) * mm, "end": v(15.13, -101.3) * mm});
            skArc(sketch, "E88.MirrorCS", {"start": v(15.13, -101.3) * mm, "mid": v(1.36, -116.3) * mm, "end": v(-14.68, -103.76) * mm});
            skSolve(sketch);
        }
        {
            var Q0;
            Q0=makeQuery(id+"F14.imprint","IMPRINT",FACE,{"disambiguationData":[TD([[makeQuery(id+"F14.imprint","IMPRINT",EDGE,{"derivedFrom":sQuery(id+"F14.wireOp",EDGE,"E74")}),-1.0]])]});
            var Q1;
            Q1=makeQuery(id+"F14.imprint","IMPRINT",FACE,{"disambiguationData":[TD([[makeQuery(id+"F14.imprint","IMPRINT",EDGE,{"derivedFrom":sQuery(id+"F14.wireOp",EDGE,"E83.MirrorC")}),1.0]])]});
            var Q2;
            Q2=makeQuery(id+"F14.imprint","IMPRINT",FACE,{"disambiguationData":[TD([[makeQuery(id+"F14.imprint","IMPRINT",EDGE,{"derivedFrom":makeQuery(id+"F1.opExtrude","CAP_EDGE",EDGE,{"disambiguationData":[OSD([sQuery(id+"F0.wireOp",EDGE,"E1.left")])],"isStart":true})}),-1.0]])]});
            extrude(context, id + "F15", {"entities" : qUnion([Q0, Q1, Q2]), "depth" : 3 * mm});
        }
    });
